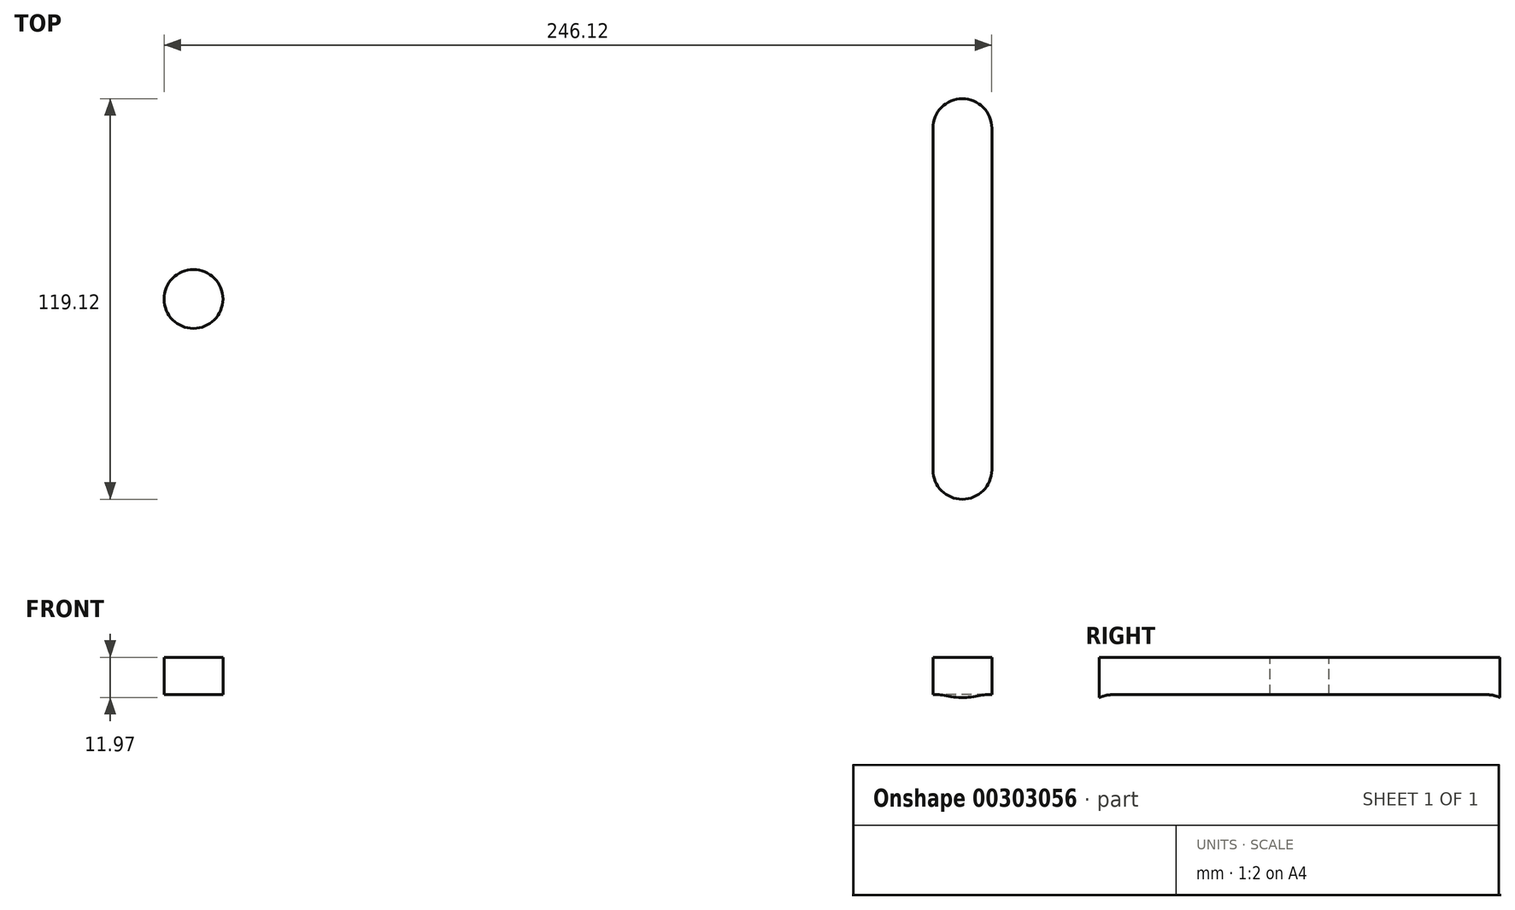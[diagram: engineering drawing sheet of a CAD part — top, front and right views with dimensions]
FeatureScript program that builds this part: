
annotation { "Feature Type Name" : "Feature", "Feature Type Description" : "" }
export const myFeature = defineFeature(function(context is Context, id is Id, definition is map)
    precondition{}
    {
        {
            var Q0;
            Q0=qCreatedBy(makeId("Right.planeOp"),FACE);
            var sketch = newSketch(context, id + "F0", { "sketchPlane" : qUnion([Q0])});
            skLineSegment(sketch, "E0.bottom", {"start": v(76.2, 27.43) * mm, "end": v(-76.2, 27.43) * mm});
            skLineSegment(sketch, "E0.left", {"start": v(76.2, 27.43) * mm, "end": v(76.2, -27.43) * mm});
            skLineSegment(sketch, "E0.right", {"start": v(-76.2, 27.43) * mm, "end": v(-76.2, -27.43) * mm});
            skPoint(sketch, "E0.middle", {"position": v(0, 0) * mm});
            skLineSegment(sketch, "E1", {"start": v(-76.2, -27.43) * mm, "end": v(-73.77, -27.43) * mm});
            skLineSegment(sketch, "E2", {"start": v(-70.92, -25.04) * mm, "end": v(-65.03, 8.39) * mm});
            skLineSegment(sketch, "E3", {"start": v(-55.56, 16.33) * mm, "end": v(55.56, 16.33) * mm});
            skArc(sketch, "E4", {"start": v(-65.03, 8.39) * mm, "mid": v(-61.74, 14.08) * mm, "end": v(-55.56, 16.33) * mm});
            skArc(sketch, "E5", {"start": v(-73.77, -27.43) * mm, "mid": v(-71.91, -26.76) * mm, "end": v(-70.92, -25.04) * mm});
            skLineSegment(sketch, "E6", {"start": v(0, 72.64) * mm, "end": v(0, -51.58) * mm, "construction": true});
            skArc(sketch, "E7.MirrorCS", {"start": v(65.03, 8.39) * mm, "mid": v(61.74, 14.08) * mm, "end": v(55.56, 16.33) * mm});
            skLineSegment(sketch, "E8.MirrorCS", {"start": v(76.2, -27.43) * mm, "end": v(73.77, -27.43) * mm});
            skLineSegment(sketch, "E9.MirrorCS", {"start": v(70.92, -25.04) * mm, "end": v(65.03, 8.39) * mm});
            skArc(sketch, "E10.MirrorCS", {"start": v(73.77, -27.43) * mm, "mid": v(71.91, -26.76) * mm, "end": v(70.92, -25.04) * mm});
            skSolve(sketch);
        }
        {
            var Q0;
            Q0=qSketchRegion(id+"F0",true);
            extrude(context, id + "F1", {"entities" : qUnion([Q0]), "depth" : 914.4 * mm, "symmetric" : true});
        }
        {
            var Q0;
            Q0=makeQuery(id+"F1.opExtrude","SWEPT_FACE",FACE,{"disambiguationData":[OSD([sQuery(id+"F0.wireOp",EDGE,"E0.bottom")])]});
            var sketch = newSketch(context, id + "F2", { "sketchPlane" : qUnion([Q0])});
            skCircle(sketch, "E11", {"center": v(-95.25, 0) * mm, "radius": 8.76 * mm});
            skLineSegment(sketch, "E12", {"start": v(-323.85, 15.6) * mm, "end": v(-323.85, -16.39) * mm, "construction": true});
            skLineSegment(sketch, "E13", {"start": v(-304.78, 0) * mm, "end": v(-341.41, 0) * mm, "construction": true});
            skLineSegment(sketch, "E14", {"start": v(-315.09, 50.8) * mm, "end": v(-315.09, -50.8) * mm});
            skLineSegment(sketch, "E15", {"start": v(-332.61, 50.8) * mm, "end": v(-332.61, -50.8) * mm});
            skArc(sketch, "E16", {"start": v(-332.61, 50.8) * mm, "mid": v(-323.85, 59.56) * mm, "end": v(-315.09, 50.8) * mm});
            skArc(sketch, "E17.MirrorCS", {"start": v(-332.61, -50.8) * mm, "mid": v(-323.85, -59.56) * mm, "end": v(-315.09, -50.8) * mm});
            skCircle(sketch, "E18.MirrorC", {"center": v(95.25, 0) * mm, "radius": 8.76 * mm});
            skArc(sketch, "E19.MirrorCS", {"start": v(332.61, -50.8) * mm, "mid": v(323.85, -59.56) * mm, "end": v(315.09, -50.8) * mm});
            skArc(sketch, "E20.MirrorCS", {"start": v(332.61, 50.8) * mm, "mid": v(323.85, 59.56) * mm, "end": v(315.09, 50.8) * mm});
            skLineSegment(sketch, "E21.MirrorCS", {"start": v(332.61, 50.8) * mm, "end": v(332.61, -50.8) * mm});
            skLineSegment(sketch, "E22.MirrorCS", {"start": v(304.78, 0) * mm, "end": v(341.41, 0) * mm, "construction": true});
            skLineSegment(sketch, "E23.MirrorCS", {"start": v(323.85, 15.6) * mm, "end": v(323.85, -16.39) * mm, "construction": true});
            skLineSegment(sketch, "E24.MirrorCS", {"start": v(315.09, 50.8) * mm, "end": v(315.09, -50.8) * mm});
            skSolve(sketch);
        }
        {
            var Q0;
            Q0=makeQuery(id+"F2.imprint","IMPRINT",FACE,{"disambiguationData":[TD([[makeQuery(id+"F2.imprint","IMPRINT",EDGE,{"derivedFrom":sQuery(id+"F2.wireOp",EDGE,"E14")}),-1.0]])]});
            var Q1;
            Q1=makeQuery(id+"F2.imprint","IMPRINT",FACE,{"disambiguationData":[TD([[makeQuery(id+"F2.imprint","IMPRINT",EDGE,{"derivedFrom":sQuery(id+"F2.wireOp",EDGE,"E11")}),1.0]])]});
            var Q2;
            Q2=makeQuery(id+"F2.imprint","IMPRINT",FACE,{"disambiguationData":[TD([[makeQuery(id+"F2.imprint","IMPRINT",EDGE,{"derivedFrom":sQuery(id+"F2.wireOp",EDGE,"E18.MirrorC")}),-1.0]])]});
            var Q3;
            Q3=makeQuery(id+"F2.imprint","IMPRINT",FACE,{"disambiguationData":[TD([[makeQuery(id+"F2.imprint","IMPRINT",EDGE,{"derivedFrom":sQuery(id+"F2.wireOp",EDGE,"E19.MirrorCS")}),-1.0]])]});
            extrude(context, id + "F3", {"entities" : qUnion([Q0, Q1, Q2, Q3]), "operationType" : NewBodyOperationType.REMOVE, "endBound" : BoundingType.THROUGH_ALL, "oppositeDirection" : true, "depth" : 25.4 * mm});
        }
    });
